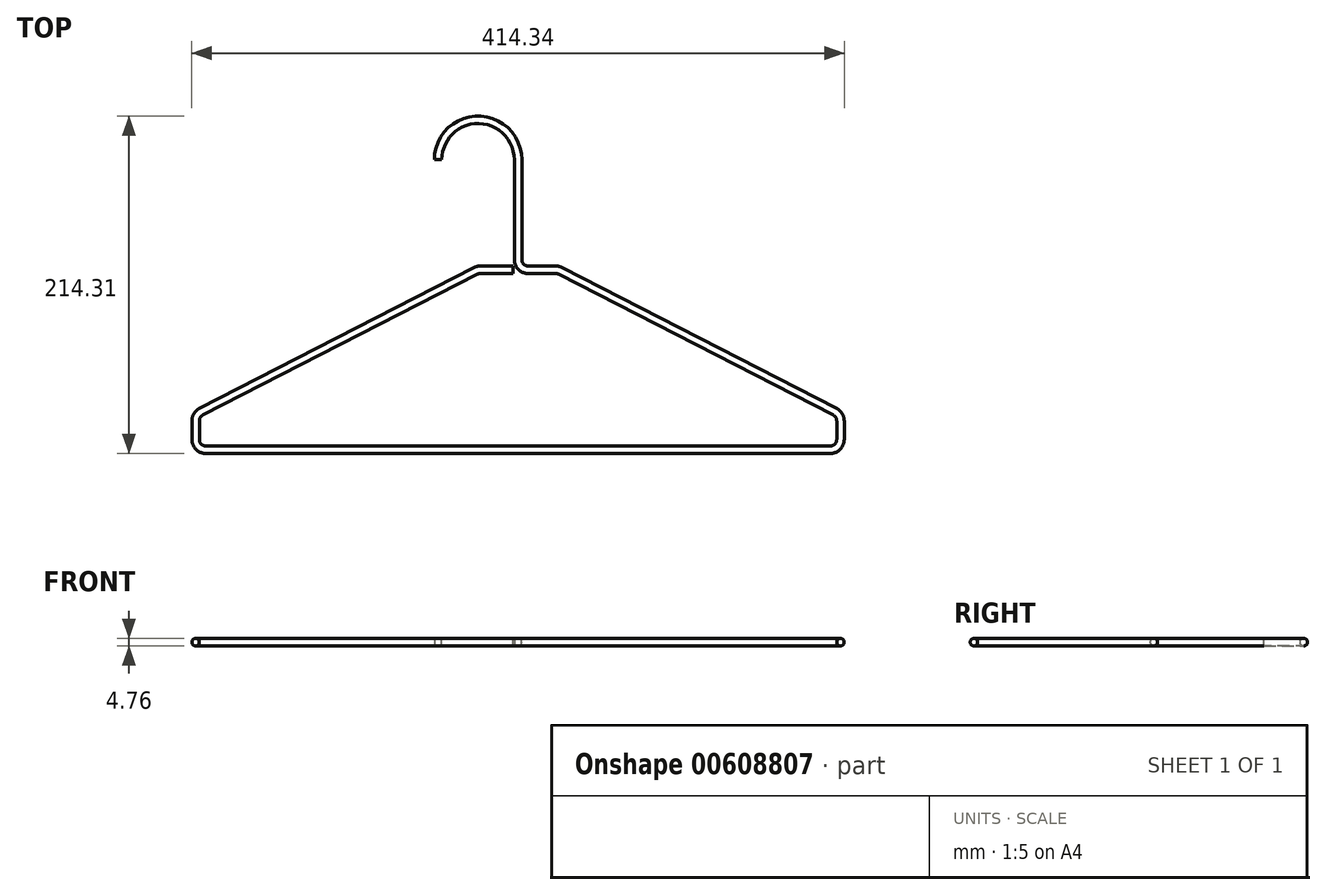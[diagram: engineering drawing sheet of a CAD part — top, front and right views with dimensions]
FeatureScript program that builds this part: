
annotation { "Feature Type Name" : "Feature", "Feature Type Description" : "" }
export const myFeature = defineFeature(function(context is Context, id is Id, definition is map)
    precondition{}
    {
        {
            var Q0;
            Q0=qCreatedBy(makeId("Front.planeOp"),FACE);
            var sketch = newSketch(context, id + "F0", { "sketchPlane" : qUnion([Q0])});
            skCircle(sketch, "E0", {"center": v(0, 0) * mm, "radius": 2.38 * mm});
            skSolve(sketch);
        }
        {
            var Q0;
            Q0=qCreatedBy(makeId("Top.planeOp"),FACE);
            var sketch = newSketch(context, id + "F1", { "sketchPlane" : qUnion([Q0])});
            skArc(sketch, "E1", {"start": v(0, 0) * mm, "mid": v(25.4, 25.4) * mm, "end": v(50.8, 0) * mm});
            skLineSegment(sketch, "E2", {"start": v(50.8, 0) * mm, "end": v(50.8, -63.5) * mm});
            skLineSegment(sketch, "E3", {"start": v(57.15, -69.85) * mm, "end": v(74.67, -69.85) * mm});
            skLineSegment(sketch, "E4", {"start": v(77.57, -70.55) * mm, "end": v(252.14, -160.15) * mm});
            skLineSegment(sketch, "E5", {"start": v(255.59, -165.8) * mm, "end": v(255.59, -177.8) * mm});
            skLineSegment(sketch, "E6", {"start": v(249.24, -184.15) * mm, "end": v(-147.64, -184.15) * mm});
            skLineSegment(sketch, "E7", {"start": v(-153.99, -177.8) * mm, "end": v(-153.99, -165.8) * mm});
            skLineSegment(sketch, "E8", {"start": v(-150.54, -160.15) * mm, "end": v(24.03, -70.55) * mm});
            skLineSegment(sketch, "E9", {"start": v(26.93, -69.85) * mm, "end": v(47.62, -69.85) * mm});
            skLineSegment(sketch, "E10", {"start": v(50.8, -69.85) * mm, "end": v(50.8, -184.15) * mm, "construction": true});
            skPoint(sketch, "E11.visualSharp", {"position": v(50.8, -69.85) * mm});
            skArc(sketch, "E11.filletArc", {"start": v(50.8, -63.5) * mm, "mid": v(52.66, -68) * mm, "end": v(57.15, -69.85) * mm});
            skPoint(sketch, "E12.visualSharp", {"position": v(76.2, -69.85) * mm});
            skArc(sketch, "E12.filletArc", {"start": v(77.57, -70.55) * mm, "mid": v(76.16, -70.03) * mm, "end": v(74.67, -69.85) * mm});
            skPoint(sketch, "E13.visualSharp", {"position": v(255.59, -161.93) * mm});
            skArc(sketch, "E13.filletArc", {"start": v(255.59, -165.8) * mm, "mid": v(254.66, -162.5) * mm, "end": v(252.14, -160.15) * mm});
            skPoint(sketch, "E14.visualSharp", {"position": v(255.59, -184.15) * mm});
            skArc(sketch, "E14.filletArc", {"start": v(249.24, -184.15) * mm, "mid": v(253.73, -182.3) * mm, "end": v(255.59, -177.8) * mm});
            skPoint(sketch, "E15.visualSharp", {"position": v(-153.99, -184.15) * mm});
            skArc(sketch, "E15.filletArc", {"start": v(-153.99, -177.8) * mm, "mid": v(-152.13, -182.3) * mm, "end": v(-147.64, -184.15) * mm});
            skPoint(sketch, "E16.visualSharp", {"position": v(-153.99, -161.93) * mm});
            skArc(sketch, "E16.filletArc", {"start": v(-150.54, -160.15) * mm, "mid": v(-153.06, -162.5) * mm, "end": v(-153.99, -165.8) * mm});
            skPoint(sketch, "E17.visualSharp", {"position": v(25.4, -69.85) * mm});
            skArc(sketch, "E17.filletArc", {"start": v(26.93, -69.85) * mm, "mid": v(25.44, -70.03) * mm, "end": v(24.03, -70.55) * mm});
            skSolve(sketch);
        }
        {
            var Q0;
            Q0 = qSketchRegion(id + "F0", true);
            var Q1;
            Q1 = qConstructionFilter(qBodyType(qCreatedBy(id + "F1" ,EDGE), BodyType.WIRE), ConstructionObject.NO);
            sweep(context, id + "F2", {"profiles" : qUnion([Q0]), "path" : qUnion([Q1])});
        }
    });
